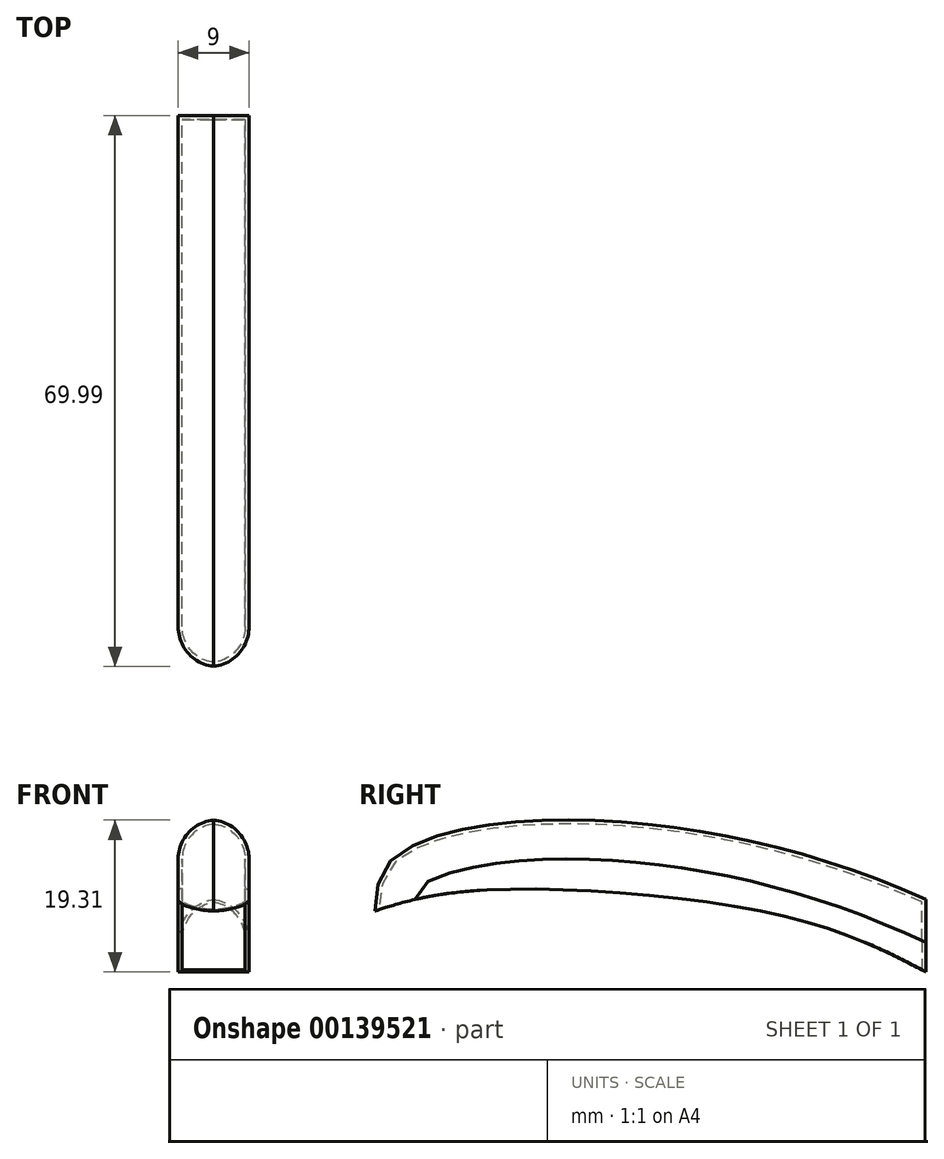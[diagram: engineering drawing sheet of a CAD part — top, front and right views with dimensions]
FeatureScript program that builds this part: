
annotation { "Feature Type Name" : "Feature", "Feature Type Description" : "" }
export const myFeature = defineFeature(function(context is Context, id is Id, definition is map)
    precondition{}
    {
        {
            var Q0;
            Q0=qCreatedBy(makeId("Right.planeOp"),FACE);
            var sketch = newSketch(context, id + "F0", { "sketchPlane" : qUnion([Q0])});
            skFitSpline(sketch, "E0", {"points": [v(-59.06, 10.23) * mm, v(-46.27, 12.8) * mm, v(-7.11, 9.58) * mm, v(10.96, 2.48) * mm], "startDerivative": vector(40.06, 12.89) * mm, "endDerivative": vector(48.08, -25.33) * mm});
            skFitSpline(sketch, "E1", {"points": [v(-59.06, 10.23) * mm, v(-55.68, 17.76) * mm, v(10.96, 11.71) * mm], "startDerivative": vector(1.66, 36.68) * mm, "endDerivative": vector(117.58, -53.13) * mm});
            skLineSegment(sketch, "E2", {"start": v(10.96, 11.71) * mm, "end": v(10.96, 2.48) * mm});
            skLineSegment(sketch, "E3", {"start": v(10.96, 0) * mm, "end": v(-59.04, 0) * mm, "construction": true});
            skLineSegment(sketch, "E4", {"start": v(-59.04, 0) * mm, "end": v(-58.91, 33.42) * mm, "construction": true});
            skSolve(sketch);
        }
        {
            var Q0;
            Q0 = qSketchRegion(id + "F0", true);
            extrude(context, id + "F1", {"entities" : qUnion([Q0]), "depth" : 9 * mm});
        }
        {
            var Q0;
            Q0=makeQuery(id+"F1.opExtrude","CAP_EDGE",EDGE,{"disambiguationData":[OSD([sQuery(id+"F0.wireOp",EDGE,"E1")])],"isStart":true});
            var Q1;
            Q1=makeQuery(id+"F1.opExtrude","CAP_EDGE",EDGE,{"disambiguationData":[OSD([sQuery(id+"F0.wireOp",EDGE,"E1")])],"isStart":false});
            fillet(context, id + "F2", {"entities" : qUnion([Q0, Q1]), "radius" : 5 * mm, "tangentPropagation" : true, "allowEdgeOverflow" : false});
        }
        {
            var Q0;
            Q0=makeQuery(id+"F1.opExtrude","SWEPT_FACE",FACE,{"disambiguationData":[OSD([sQuery(id+"F0.wireOp",EDGE,"E0")])]});
            shell(context, id + "F3", {"entities" : qUnion([Q0]), "thickness" : 0.5 * mm});
        }
    });
